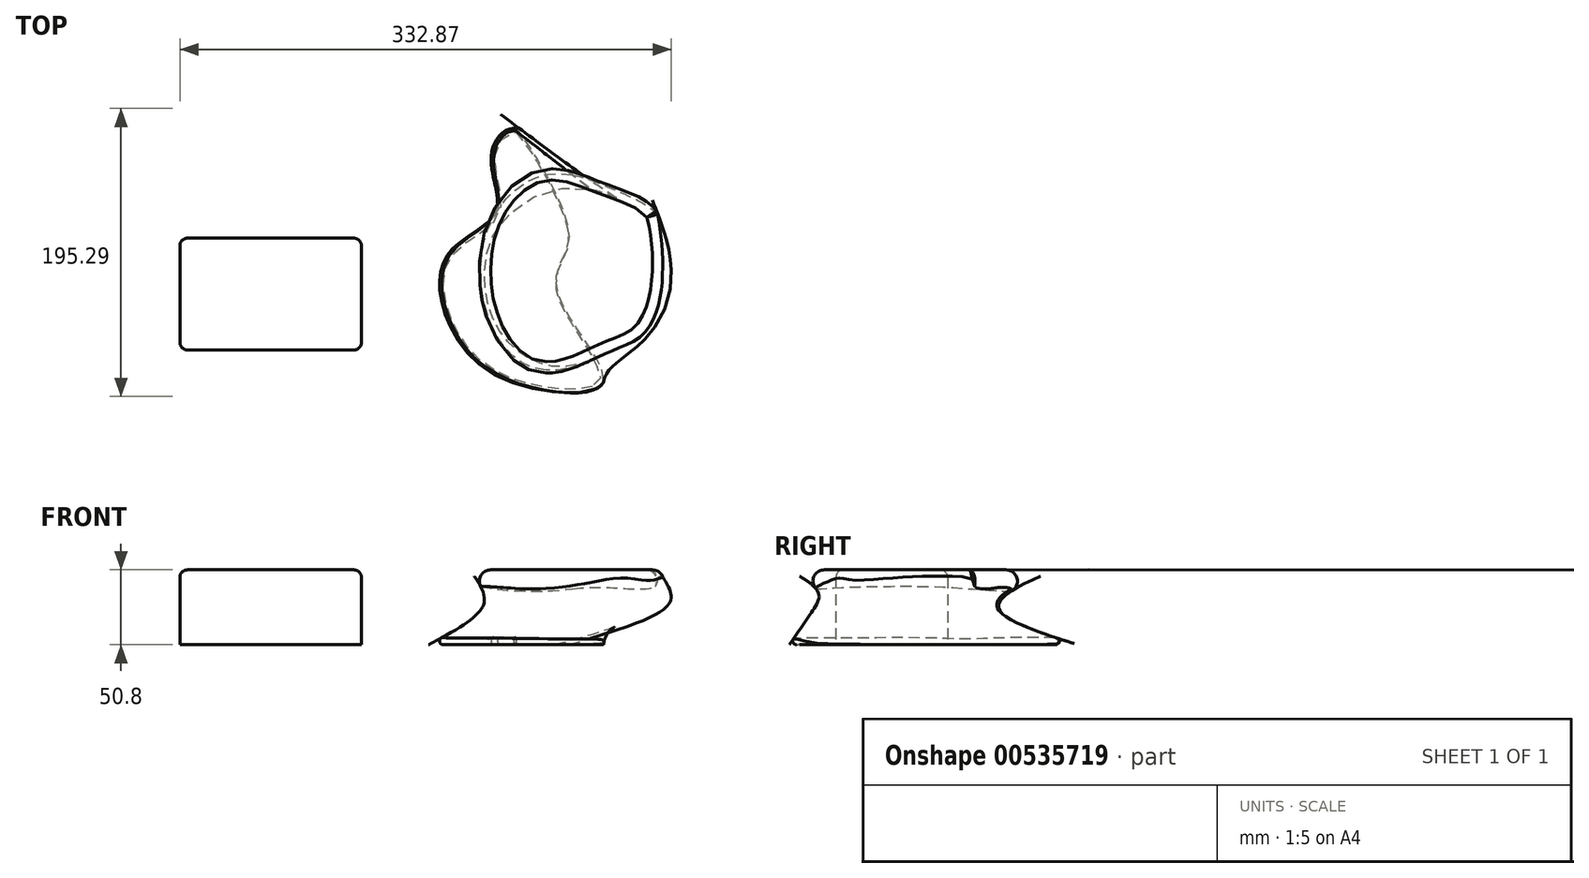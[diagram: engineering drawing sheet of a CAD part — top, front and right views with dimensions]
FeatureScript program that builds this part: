
annotation { "Feature Type Name" : "Feature", "Feature Type Description" : "" }
export const myFeature = defineFeature(function(context is Context, id is Id, definition is map)
    precondition{}
    {
        {
            var Q0;
            Q0=qCreatedBy(makeId("Top.planeOp"),FACE);
            var sketch = newSketch(context, id + "F0", { "sketchPlane" : qUnion([Q0])});
            skLineSegment(sketch, "E0.bottom", {"start": v(61.49, 37.9) * mm, "end": v(-61.49, 37.9) * mm});
            skLineSegment(sketch, "E0.top", {"start": v(61.49, -37.9) * mm, "end": v(-61.49, -37.9) * mm});
            skLineSegment(sketch, "E0.left", {"start": v(61.49, 37.9) * mm, "end": v(61.49, -37.9) * mm});
            skLineSegment(sketch, "E0.right", {"start": v(-61.49, 37.9) * mm, "end": v(-61.49, -37.9) * mm});
            skPoint(sketch, "E0.middle", {"position": v(0, 0) * mm});
            skSolve(sketch);
        }
        {
            var Q0;
            Q0=makeQuery(id+"F0.imprint","IMPRINT",FACE,{"disambiguationData":[TD([[makeQuery(id+"F0.imprint","IMPRINT",EDGE,{"derivedFrom":sQuery(id+"F0.wireOp",EDGE,"E0.bottom")}),1.0]])]});
            extrude(context, id + "F1", {"entities" : qUnion([Q0]), "depth" : 50.8 * mm, "offsetDistance" : 25.4 * mm});
        }
        {
            var Q0;
            Q0=makeQuery(id+"F1.opExtrude","CAP_EDGE",EDGE,{"disambiguationData":[OSD([sQuery(id+"F0.wireOp",EDGE,"E0.left")])],"isStart":false});
            var Q1;
            Q1=makeQuery(id+"F1.opExtrude","CAP_EDGE",EDGE,{"disambiguationData":[OSD([sQuery(id+"F0.wireOp",EDGE,"E0.top")])],"isStart":false});
            var Q2;
            Q2=makeQuery(id+"F1.opExtrude","CAP_EDGE",EDGE,{"disambiguationData":[OSD([sQuery(id+"F0.wireOp",EDGE,"E0.right")])],"isStart":false});
            var Q3;
            Q3=makeQuery(id+"F1.opExtrude","CAP_EDGE",EDGE,{"disambiguationData":[OSD([sQuery(id+"F0.wireOp",EDGE,"E0.bottom")])],"isStart":false});
            var Q4;
            Q4=makeQuery(id+"F1.opExtrude","SWEPT_EDGE",EDGE,{"disambiguationData":[OSD([sQuery(id+"F0.wireOp",EDGE,"E0.top"),sQuery(id+"F0.wireOp",EDGE,"E0.right")])]});
            var Q5;
            Q5=makeQuery(id+"F1.opExtrude","SWEPT_EDGE",EDGE,{"disambiguationData":[OSD([sQuery(id+"F0.wireOp",EDGE,"E0.top"),sQuery(id+"F0.wireOp",EDGE,"E0.left")])]});
            var Q6;
            Q6=makeQuery(id+"F1.opExtrude","SWEPT_EDGE",EDGE,{"disambiguationData":[OSD([sQuery(id+"F0.wireOp",EDGE,"E0.bottom"),sQuery(id+"F0.wireOp",EDGE,"E0.left")])]});
            var Q7;
            Q7=makeQuery(id+"F1.opExtrude","SWEPT_EDGE",EDGE,{"disambiguationData":[OSD([sQuery(id+"F0.wireOp",EDGE,"E0.bottom"),sQuery(id+"F0.wireOp",EDGE,"E0.right")])]});
            fillet(context, id + "F2", {"entities" : qUnion([Q0, Q1, Q2, Q3, Q4, Q5, Q6, Q7]), "radius" : 5.08 * mm, "tangentPropagation" : true, "allowEdgeOverflow" : false});
        }
        {
            var Q0;
            Q0=qCreatedBy(makeId("Top.planeOp"),FACE);
            var sketch = newSketch(context, id + "F3", { "sketchPlane" : qUnion([Q0])});
            skFitSpline(sketch, "E1", {"points": [v(150.18, 56.04) * mm, v(111.51, 25.1) * mm, v(124.34, -39.85) * mm, v(178.21, -67.2) * mm, v(225.25, -61.11) * mm, v(194.37, 0) * mm, v(199.33, 26.93) * mm, v(199.3, 52.3) * mm, v(147.66, 125.97) * mm, v(135.35, 104.97) * mm, v(150.18, 56.04) * mm]});
            skSolve(sketch);
        }
        {
            var Q0;
            Q0=qCreatedBy(makeId("Top.planeOp"),FACE);
            cPlane(context, id + "F4", {"entities" : qUnion([Q0]), "cplaneType" : CPlaneType.OFFSET, "offset" : 25.4 * mm, "width" : 152.4 * mm, "height" : 152.4 * mm});
        }
        {
            var Q0;
            Q0=qCreatedBy(id+"F4.planeOp",FACE);
            cPlane(context, id + "F5", {"entities" : qUnion([Q0]), "cplaneType" : CPlaneType.OFFSET, "offset" : 25.4 * mm, "width" : 152.4 * mm, "height" : 152.4 * mm});
        }
        {
            var Q0;
            Q0=qCreatedBy(id+"F4.planeOp",FACE);
            var sketch = newSketch(context, id + "F6", { "sketchPlane" : qUnion([Q0])});
            skCircle(sketch, "E2", {"center": v(205.64, 10.04) * mm, "radius": 62.26 * mm});
            skSolve(sketch);
        }
        {
            var Q0;
            Q0=qCreatedBy(id+"F5.planeOp",FACE);
            var sketch = newSketch(context, id + "F7", { "sketchPlane" : qUnion([Q0])});
            skFitSpline(sketch, "E3", {"points": [v(137.67, 58.71) * mm, v(140.1, -19.83) * mm, v(182.62, -69.27) * mm, v(231.44, -38.24) * mm, v(259, -18.93) * mm, v(257.85, 63.5) * mm, v(240.34, 89.65) * mm, v(206, 91.96) * mm, v(152.42, 109.33) * mm, v(137.67, 58.71) * mm]});
            skSolve(sketch);
        }
        {
            var Q0;
            Q0 = qSketchRegion(id + "F3", true);
            var Q1;
            Q1 = qSketchRegion(id + "F6", true);
            var Q2;
            Q2 = qSketchRegion(id + "F7", true);
            loft(context, id + "F8", {"sheetProfilesArray" : [{ "sheetProfileEntities" : qUnion([Q0]) }, { "sheetProfileEntities" : qUnion([Q1]) }, { "sheetProfileEntities" : qUnion([Q2]) }]});
        }
        {
            var Q0;
            Q0=makeQuery(id+"F8.opLoft","MID_CAP_EDGE",EDGE,{"disambiguationData":[OSD([sQuery(id+"F3.wireOp",EDGE,"E1"),sQuery(id+"F7.wireOp",EDGE,"E3")])],"capPos":2.0});
            fillet(context, id + "F9", {"entities" : qUnion([Q0]), "radius" : 7.62 * mm, "tangentPropagation" : true, "allowEdgeOverflow" : false});
        }
        {
            var Q0;
            Q0=makeQuery(id+"F8.opLoft","MID_CAP_EDGE",EDGE,{"disambiguationData":[OSD([sQuery(id+"F3.wireOp",EDGE,"E1")])],"capPos":0.0});
            fillet(context, id + "F10", {"entities" : qUnion([Q0]), "radius" : 2.54 * mm, "allowEdgeOverflow" : false});
        }
    });
